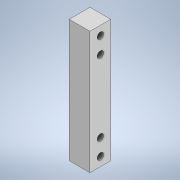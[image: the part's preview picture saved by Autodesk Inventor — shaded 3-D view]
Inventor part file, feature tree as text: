
AUTODESK INVENTOR PART (.ipt)
format: ipt  version: 2022 (Build 260153000, 153)  size: 112,640 bytes
history: native  units: in
note: dims shown in document units (in); Inventor stores cm internally (conversion verified against a paired STEP export)
features: extrude x2, sketch x2
ambient origin geometry x8: Origin, YZ Plane, XZ Plane, XY Plane, X Axis, Y Axis, Z Axis, Center Point
bodies: Solid1 (feature_tree)
feature tree (4):
  extrude  "Extrusion1"  Depth=0.5in
  extrude  "Extrusion2"  Depth=0.3937in
  sketch  "Sketch2"  dims[d0=2.9528in d1=0.5in]
  sketch  "Sketch3"  dims[d2=0.5in d3=0.0in d4=0.8661in d5=0.3937in d6=0.1575in d7=0.0in d8=0.0in]
